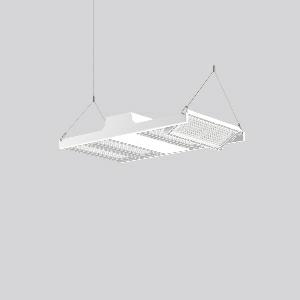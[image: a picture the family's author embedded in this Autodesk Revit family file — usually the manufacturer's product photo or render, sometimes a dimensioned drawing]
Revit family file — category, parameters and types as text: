
# Revit family: light_case_921687_002_76_c906
name_source: partatom
category: Lighting Fixtures
units: mm (PartAtom-declared; Revit-internal decimal feet)

## family parameters
Cut with Voids When Loaded = No
Host = Face
Light Source = No
Part Type = Normal
Room Calculation Point = No
Round Connector Dimension = Use Diameter
Shared = No

## types (1)
- LIGHT CASE (1 x LED Modul 840, 8850 lm, 4000)
    Apparent Load = 225 VA
    CIE Flux Codes = 85 97 100 100 100
    Color Rendering = 80
    Color Temperature = 4000
    Default Elevation = 1800 mm
    Description = Series: LIGHT CASE
Flat highbay luminaire for chain or cable suspension with 4 LED modules that can be swivelled. Housing: die cast aluminium and sheet steel, powder-coated. Optimised thermal management thanks to special luminaire design. Self-cleaning heat sink for constant heat dissipation. Cover: plastic (polycarbonate, shockproof), with integrated four-row lens system. LED modules can be swivelled ± 30° for optimum illumination. Suitable for chain or steel cable suspension (to be provided on site). With 5-pin connection terminal (1.5 m). With integrated movement sensor and light sensor for daylight detection on request. Ball impact proof in accordance with DIN 18032-03 (except steel cable suspension). Luminaire with limited surface temperature in accordance with EN 60598-2-24 for use in environments in which a deposit of conductive dust on the luminaire can be expected. 
Colour: white
Length: 680 mm
Width: 397 mm
Height: 110 mm
Lamp: LED
Socket: without socket
Colour temperature: 4000K
Colour rendering index (CRI): 80
System power: 225 W
Rated luminous flux: 35400 lm
Luminous efficiency: 157 lm/W
Control gear: Converter, dimmable, DALI
Protection class: I
Type of protection: IP 65
    Height = 110 mm
    Lamp = 1 x LED Modul 840
    Lamp Light Flux = 8850 lm
    Lamp count = 1
    Length = 680 mm
    Lifetime = 50000 h
    Luminous efficacy = 157 lm/W
    Manufacturer = RZB
    ModVariant = No
    Model = 921687.002.76
    Mounting Place = Ceiling
    Mounting Type = Pendant
    Number of Poles = 1
    OnlyDefault = Yes
    Power Factor = 1
    Product Name = LIGHT CASE
    Product group = Pendant commercial luminaires
    ProductGroupID = 903
    Protection Class = Protection class I
    Protection Degree = IP 65
    RLX_Detail_Level = 1
    RLX_Emergency_Light_Flux = 0 lm
    RLX_Emergency_Type = 0
    RLX_Emergency_Type_DB = No
    RlxData = <blob elided: 28065 chars, md5=2d742464>
    Socket = socket
    Standby Power = 0 W
    System Light Flux = 35400 lm
    System Power = 225 W
    Type Comments = Product without accessories
    Type Image = 921523.002.76.jpg
    URL = http://relux.com
    VarID = ---
    Voltage = 230 V
    Voltage Range = 220-240 V
    Weight = 0.00 kg
    Width = 397 mm

## geometry (parser evidence)
native form markers: Blend x4, Sweep x21
no freeform markers — native parametric forms only
